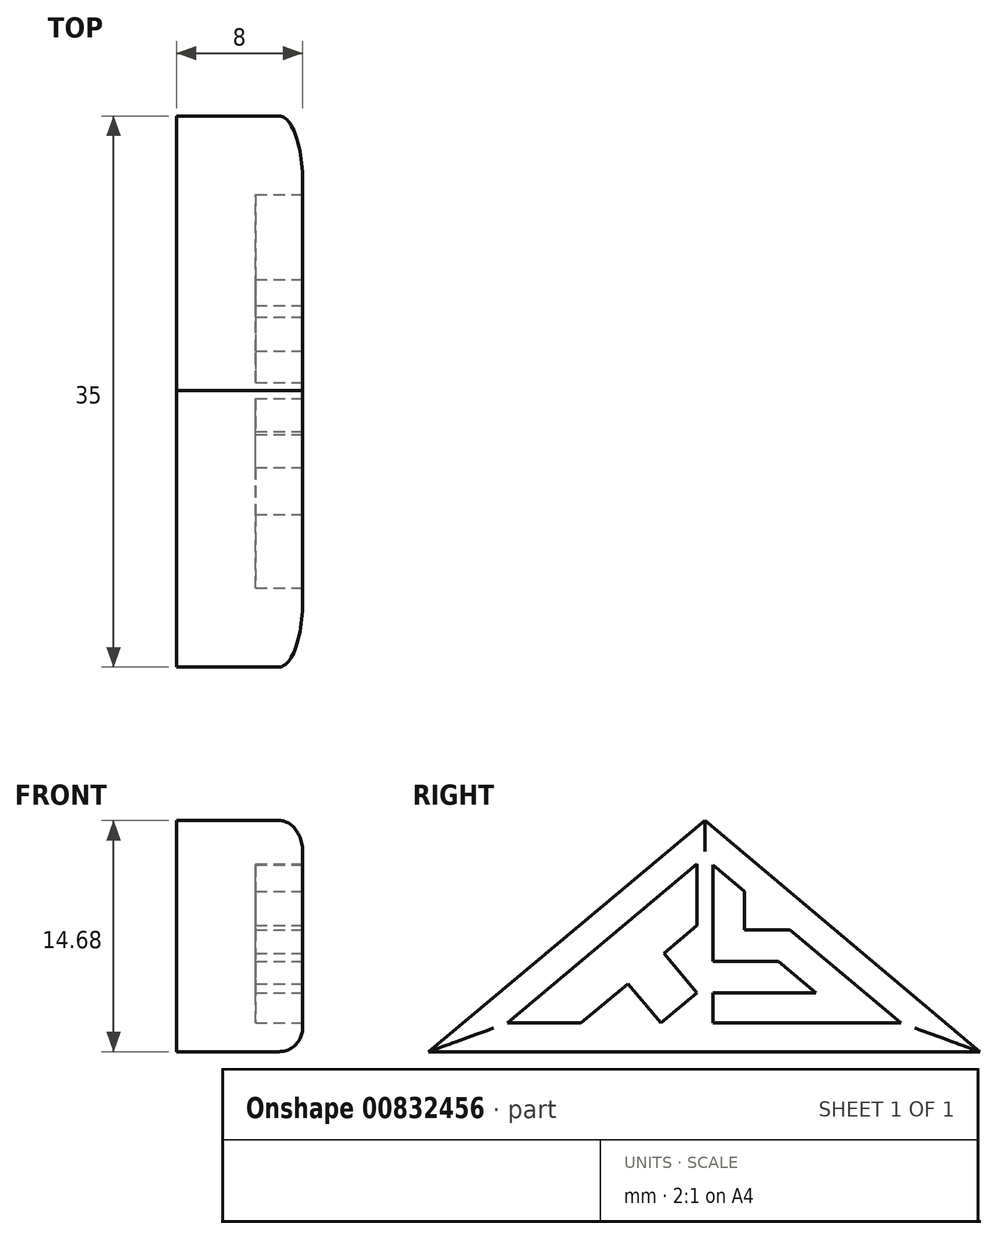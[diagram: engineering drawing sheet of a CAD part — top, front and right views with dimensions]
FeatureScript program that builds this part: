
annotation { "Feature Type Name" : "Feature", "Feature Type Description" : "" }
export const myFeature = defineFeature(function(context is Context, id is Id, definition is map)
    precondition{}
    {
        {
            var Q0;
            Q0=qCreatedBy(makeId("Right.planeOp"),FACE);
            var sketch = newSketch(context, id + "F0", { "sketchPlane" : qUnion([Q0])});
            skLineSegment(sketch, "E0", {"start": v(-17.56, 0) * mm, "end": v(0, 14.68) * mm});
            skLineSegment(sketch, "E1", {"start": v(0, 14.68) * mm, "end": v(17.44, 0) * mm});
            skLineSegment(sketch, "E2", {"start": v(17.44, 0) * mm, "end": v(-17.56, 0) * mm});
            skSolve(sketch);
        }
        {
            var Q0;
            Q0=makeQuery(id+"F0.imprint","IMPRINT",FACE,{"disambiguationData":[TD([[makeQuery(id+"F0.imprint","IMPRINT",EDGE,{"derivedFrom":sQuery(id+"F0.wireOp",EDGE,"E0")}),-1.0]])]});
            extrude(context, id + "F1", {"entities" : qUnion([Q0]), "depth" : 8 * mm, "offsetDistance" : 25 * mm});
        }
        {
            var Q0;
            Q0=makeQuery(id+"F1.opExtrude","CAP_FACE",FACE,{"disambiguationData":[OSD([sQuery(id+"F0.wireOp",EDGE,"E0"),sQuery(id+"F0.wireOp",EDGE,"E1"),sQuery(id+"F0.wireOp",EDGE,"E2")])],"isStart":false});
            var sketch = newSketch(context, id + "F2", { "sketchPlane" : qUnion([Q0])});
            skLineSegment(sketch, "E3", {"start": v(-12.54, 1.82) * mm, "end": v(-0.04, 12.3) * mm});
            skLineSegment(sketch, "E4", {"start": v(-0.04, 12.3) * mm, "end": v(12.46, 1.82) * mm});
            skLineSegment(sketch, "E5", {"start": v(12.46, 1.82) * mm, "end": v(-12.54, 1.82) * mm});
            skLineSegment(sketch, "E6", {"start": v(-4.9, 4.32) * mm, "end": v(-7.88, 1.82) * mm});
            skLineSegment(sketch, "E7", {"start": v(-7.88, 1.82) * mm, "end": v(-12.54, 1.82) * mm});
            skLineSegment(sketch, "E8", {"start": v(-4.9, 4.32) * mm, "end": v(-2.8, 1.82) * mm});
            skLineSegment(sketch, "E9", {"start": v(4.66, 5.75) * mm, "end": v(7.05, 3.75) * mm});
            skLineSegment(sketch, "E10", {"start": v(2.5, 10.17) * mm, "end": v(2.5, 7.75) * mm});
            skLineSegment(sketch, "E11", {"start": v(2.5, 7.75) * mm, "end": v(5.4, 7.75) * mm});
            skLineSegment(sketch, "E12", {"start": v(-0.5, 11.93) * mm, "end": v(-0.5, 1.82) * mm});
            skLineSegment(sketch, "E13", {"start": v(-0.5, 1.82) * mm, "end": v(0.5, 1.82) * mm});
            skLineSegment(sketch, "E14", {"start": v(0.5, 1.82) * mm, "end": v(0.5, 11.85) * mm});
            skLineSegment(sketch, "E15", {"start": v(7.05, 3.75) * mm, "end": v(0.5, 3.75) * mm});
            skLineSegment(sketch, "E16", {"start": v(4.66, 5.75) * mm, "end": v(0.5, 5.75) * mm});
            skLineSegment(sketch, "E17", {"start": v(-2.8, 1.82) * mm, "end": v(-0.5, 3.75) * mm});
            skLineSegment(sketch, "E18", {"start": v(-0.5, 3.75) * mm, "end": v(-2.6, 6.25) * mm});
            skLineSegment(sketch, "E19", {"start": v(-2.6, 6.25) * mm, "end": v(-0.5, 8) * mm});
            skSolve(sketch);
        }
        {
            var Q0;
            {var subQ0=sQuery(id+"F2.wireOp",EDGE,"E3");Q0=makeQuery(id+"F2.imprint","IMPRINT",FACE,{"disambiguationData":[TD([[makeQuery(id+"F2.imprint","IMPRINT",EDGE,{"derivedFrom":subQ0}),-1.0]])]});}
            var Q1;
            Q1=makeQuery(id+"F2.imprint","IMPRINT",FACE,{"disambiguationData":[TD([[makeQuery(id+"F2.imprint","IMPRINT",EDGE,{"derivedFrom":sQuery(id+"F2.wireOp",EDGE,"E9")}),1.0]])]});
            extrude(context, id + "F3", {"entities" : qUnion([Q0, Q1]), "operationType" : NewBodyOperationType.REMOVE, "oppositeDirection" : true, "depth" : 3 * mm, "offsetDistance" : 25 * mm});
        }
        {
            var Q0;
            Q0=makeQuery(id+"F1.opExtrude","CAP_EDGE",EDGE,{"disambiguationData":[OSD([sQuery(id+"F0.wireOp",EDGE,"E1")])],"isStart":false});
            var Q1;
            Q1=makeQuery(id+"F1.opExtrude","CAP_EDGE",EDGE,{"disambiguationData":[OSD([sQuery(id+"F0.wireOp",EDGE,"E0")])],"isStart":false});
            var Q2;
            Q2=makeQuery(id+"F1.opExtrude","CAP_EDGE",EDGE,{"disambiguationData":[OSD([sQuery(id+"F0.wireOp",EDGE,"E2")])],"isStart":false});
            fillet(context, id + "F4", {"entities" : qUnion([Q0, Q1, Q2]), "radius" : 1.5 * mm, "tangentPropagation" : true, "allowEdgeOverflow" : false});
        }
    });
